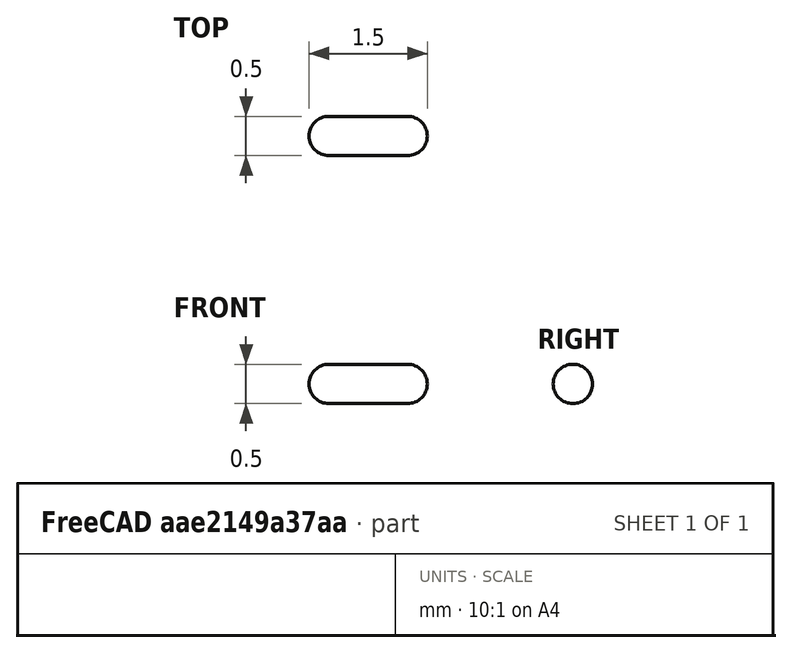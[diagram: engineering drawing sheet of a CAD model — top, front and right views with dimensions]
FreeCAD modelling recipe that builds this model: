
FCSTD DOCUMENT  (FreeCAD 0.16R6712 (Git))
Label: minus
License: All rights reserved
LicenseURL: http://en.wikipedia.org/wiki/All_rights_reserved
objects: Sketcher::SketchObject×1, PartDesign::Revolution×1, Mesh::Feature×1
note: 3 computed .brp shape members not serialized (recipe doc carries the construction recipe); baked Part::Feature solids carry a one-line shape summary decoded from their .brp

FEATURE [Sketcher::SketchObject] Sketch
  sketch-geometry (4):
    g0: LineSegment StartX=-0.500001 StartY=0.25 StartZ=0 EndX=0.5 EndY=0.25 EndZ=0
    g1: ArcOfCircle CenterX=-0.500001 CenterY=0 CenterZ=0 NormalX=0 NormalY=0 NormalZ=1 Radius=0.25 StartAngle=1.5708 EndAngle=3.14159
    g2: ArcOfCircle CenterX=0.500001 CenterY=0 CenterZ=0 NormalX=0 NormalY=0 NormalZ=1 Radius=0.25 StartAngle=0 EndAngle=1.5708
    g3: LineSegment StartX=-0.750001 StartY=0 StartZ=0 EndX=0.750001 EndY=0 EndZ=0
  constraints (14):
    c: Horizontal(g0)
    c: PointOnObject(g1,g-1)
    c: Coincident(g2,g0)
    c: Coincident(g0,g1)
    c: PointOnObject(g2,g-1)
    c: PointOnObject(g1,g-1)
    c: Tangent(g1,g0)
    c: Tangent(g0,g2)
    c: Coincident(g3,g1)
    c: Coincident(g3,g2)
    c: Symmetric(g1,g2,g-2)
    c: Equal(g2,g1)
    c: DistanceX(g-2,g0) = 0.5
    c: Distance(g-1,g0) = 0.25
FEATURE [PartDesign::Revolution] Revolution
  Angle = 360
  Axis = (1,0,0)
  Base = (0,0,0)
  ReferenceAxis = -> Sketch [H_Axis]
  Sketch = -> Sketch
FEATURE [Mesh::Feature] Mesh  label="Revolution (Meshed)"
